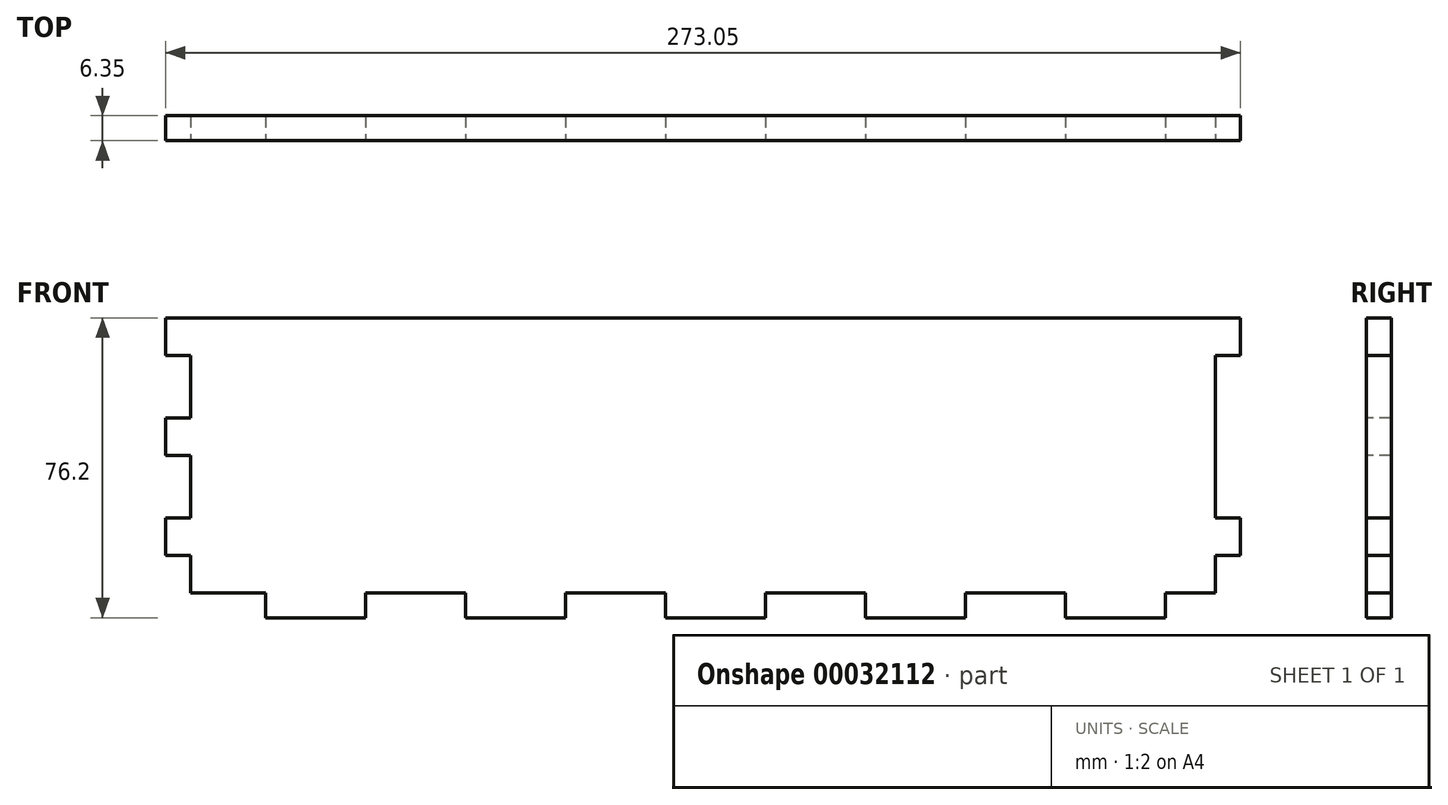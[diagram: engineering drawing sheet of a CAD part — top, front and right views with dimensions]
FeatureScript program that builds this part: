
annotation { "Feature Type Name" : "Feature", "Feature Type Description" : "" }
export const myFeature = defineFeature(function(context is Context, id is Id, definition is map)
    precondition{}
    {
        {
            var Q0;
            Q0=qCreatedBy(makeId("Front.planeOp"),FACE);
            var sketch = newSketch(context, id + "F0", { "sketchPlane" : qUnion([Q0])});
            skLineSegment(sketch, "E0.bottom", {"start": v(0, 0) * mm, "end": v(273.05, 0) * mm});
            skLineSegment(sketch, "E0.top", {"start": v(0, 76.2) * mm, "end": v(273.05, 76.2) * mm});
            skLineSegment(sketch, "E0.left", {"start": v(0, 0) * mm, "end": v(0, 76.2) * mm});
            skLineSegment(sketch, "E0.right", {"start": v(273.05, 0) * mm, "end": v(273.05, 76.2) * mm});
            skSolve(sketch);
        }
        {
            var Q0;
            Q0=makeQuery(id+"F0.imprint","IMPRINT",FACE,{"disambiguationData":[TD([[makeQuery(id+"F0.imprint","IMPRINT",EDGE,{"derivedFrom":sQuery(id+"F0.wireOp",EDGE,"E0.bottom")}),1.0]])]});
            extrude(context, id + "F1", {"entities" : qUnion([Q0]), "depth" : 6.35 * mm});
        }
        {
            var Q0;
            Q0=makeQuery(id+"F1.opExtrude","CAP_FACE",FACE,{"disambiguationData":[OSD([sQuery(id+"F0.wireOp",EDGE,"E0.bottom"),sQuery(id+"F0.wireOp",EDGE,"E0.top"),sQuery(id+"F0.wireOp",EDGE,"E0.left"),sQuery(id+"F0.wireOp",EDGE,"E0.right")])],"isStart":false});
            var sketch = newSketch(context, id + "F2", { "sketchPlane" : qUnion([Q0])});
            skLineSegment(sketch, "E1.bottom", {"start": v(0, 66.68) * mm, "end": v(6.35, 66.68) * mm});
            skLineSegment(sketch, "E1.top", {"start": v(0, 50.8) * mm, "end": v(6.35, 50.8) * mm});
            skLineSegment(sketch, "E1.left", {"start": v(0, 66.68) * mm, "end": v(0, 50.8) * mm});
            skLineSegment(sketch, "E1.right", {"start": v(6.35, 66.68) * mm, "end": v(6.35, 50.8) * mm});
            skLineSegment(sketch, "E2.bottom", {"start": v(0, 41.28) * mm, "end": v(6.35, 41.28) * mm});
            skLineSegment(sketch, "E2.top", {"start": v(0, 25.4) * mm, "end": v(6.35, 25.4) * mm});
            skLineSegment(sketch, "E2.left", {"start": v(0, 41.28) * mm, "end": v(0, 25.4) * mm});
            skLineSegment(sketch, "E2.right", {"start": v(6.35, 41.28) * mm, "end": v(6.35, 25.4) * mm});
            skLineSegment(sketch, "E3.bottom", {"start": v(0, 15.88) * mm, "end": v(6.35, 15.88) * mm});
            skLineSegment(sketch, "E3.top", {"start": v(0, 6.35) * mm, "end": v(6.35, 6.35) * mm});
            skLineSegment(sketch, "E3.left", {"start": v(0, 15.88) * mm, "end": v(0, 6.35) * mm});
            skLineSegment(sketch, "E3.right", {"start": v(6.35, 15.88) * mm, "end": v(6.35, 6.35) * mm});
            skLineSegment(sketch, "E4", {"start": v(136.53, 76.2) * mm, "end": v(136.53, 0) * mm, "construction": true});
            skLineSegment(sketch, "E5.MirrorCS", {"start": v(266.7, 15.88) * mm, "end": v(266.7, 6.35) * mm});
            skLineSegment(sketch, "E6.MirrorCS", {"start": v(273.05, 15.88) * mm, "end": v(273.05, 6.35) * mm});
            skLineSegment(sketch, "E7.MirrorCS", {"start": v(273.05, 6.35) * mm, "end": v(266.7, 6.35) * mm});
            skLineSegment(sketch, "E8.MirrorCS", {"start": v(273.05, 15.88) * mm, "end": v(266.7, 15.88) * mm});
            skLineSegment(sketch, "E9.MirrorCS", {"start": v(273.05, 41.28) * mm, "end": v(266.7, 41.28) * mm});
            skLineSegment(sketch, "E10.MirrorCS", {"start": v(273.05, 25.4) * mm, "end": v(266.7, 25.4) * mm});
            skLineSegment(sketch, "E11.MirrorCS", {"start": v(273.05, 66.68) * mm, "end": v(266.7, 66.68) * mm});
            skLineSegment(sketch, "E12.MirrorCS", {"start": v(273.05, 50.8) * mm, "end": v(266.7, 50.8) * mm});
            skLineSegment(sketch, "E13.MirrorCS", {"start": v(266.7, 41.28) * mm, "end": v(266.7, 25.4) * mm});
            skLineSegment(sketch, "E14.MirrorCS", {"start": v(273.05, 41.28) * mm, "end": v(273.05, 25.4) * mm});
            skLineSegment(sketch, "E15.MirrorCS", {"start": v(266.7, 66.68) * mm, "end": v(266.7, 50.8) * mm});
            skLineSegment(sketch, "E16.MirrorCS", {"start": v(273.05, 66.68) * mm, "end": v(273.05, 50.8) * mm});
            skSolve(sketch);
        }
        {
            var Q0;
            Q0=qSketchRegion(id+"F2",true);
            extrude(context, id + "F3", {"entities" : qUnion([Q0]), "operationType" : NewBodyOperationType.REMOVE, "endBound" : BoundingType.UP_TO_NEXT, "oppositeDirection" : true, "depth" : 25.4 * mm});
        }
        {
            var Q0;
            Q0=makeQuery(id+"F1.opExtrude","CAP_FACE",FACE,{"disambiguationData":[OSD([sQuery(id+"F0.wireOp",EDGE,"E0.bottom"),sQuery(id+"F0.wireOp",EDGE,"E0.top"),sQuery(id+"F0.wireOp",EDGE,"E0.left"),sQuery(id+"F0.wireOp",EDGE,"E0.right")])],"isStart":false});
            var sketch = newSketch(context, id + "F4", { "sketchPlane" : qUnion([Q0])});
            skLineSegment(sketch, "E17.bottom", {"start": v(0, 0) * mm, "end": v(25.4, 0) * mm});
            skLineSegment(sketch, "E17.top", {"start": v(0, 6.35) * mm, "end": v(25.4, 6.35) * mm});
            skLineSegment(sketch, "E17.left", {"start": v(0, 0) * mm, "end": v(0, 6.35) * mm});
            skLineSegment(sketch, "E17.right", {"start": v(25.4, 0) * mm, "end": v(25.4, 6.35) * mm});
            skLineSegment(sketch, "E18.1.0.0", {"start": v(76.2, 0) * mm, "end": v(76.2, 6.35) * mm});
            skLineSegment(sketch, "E18.1.0.1", {"start": v(50.8, 0) * mm, "end": v(50.8, 6.35) * mm});
            skLineSegment(sketch, "E18.1.0.2", {"start": v(50.8, 6.35) * mm, "end": v(76.2, 6.35) * mm});
            skLineSegment(sketch, "E18.1.0.3", {"start": v(50.8, 0) * mm, "end": v(76.2, 0) * mm});
            skLineSegment(sketch, "E18.2.0.0", {"start": v(127, 0) * mm, "end": v(127, 6.35) * mm});
            skLineSegment(sketch, "E18.2.0.1", {"start": v(101.6, 0) * mm, "end": v(101.6, 6.35) * mm});
            skLineSegment(sketch, "E18.2.0.2", {"start": v(101.6, 6.35) * mm, "end": v(127, 6.35) * mm});
            skLineSegment(sketch, "E18.2.0.3", {"start": v(101.6, 0) * mm, "end": v(127, 0) * mm});
            skLineSegment(sketch, "E18.3.0.0", {"start": v(177.8, 0) * mm, "end": v(177.8, 6.35) * mm});
            skLineSegment(sketch, "E18.3.0.1", {"start": v(152.4, 0) * mm, "end": v(152.4, 6.35) * mm});
            skLineSegment(sketch, "E18.3.0.2", {"start": v(152.4, 6.35) * mm, "end": v(177.8, 6.35) * mm});
            skLineSegment(sketch, "E18.3.0.3", {"start": v(152.4, 0) * mm, "end": v(177.8, 0) * mm});
            skLineSegment(sketch, "E18.4.0.0", {"start": v(228.6, 0) * mm, "end": v(228.6, 6.35) * mm});
            skLineSegment(sketch, "E18.4.0.1", {"start": v(203.2, 0) * mm, "end": v(203.2, 6.35) * mm});
            skLineSegment(sketch, "E18.4.0.2", {"start": v(203.2, 6.35) * mm, "end": v(228.6, 6.35) * mm});
            skLineSegment(sketch, "E18.4.0.3", {"start": v(203.2, 0) * mm, "end": v(228.6, 0) * mm});
            skLineSegment(sketch, "E18.direction1", {"start": v(25.4, 0) * mm, "end": v(76.2, 0) * mm, "construction": true});
            skLineSegment(sketch, "E19.0.5.0", {"start": v(279.4, 0) * mm, "end": v(279.4, 6.35) * mm});
            skLineSegment(sketch, "E19.3.5.0", {"start": v(254, 0) * mm, "end": v(254, 6.35) * mm});
            skLineSegment(sketch, "E19.6.5.0", {"start": v(254, 6.35) * mm, "end": v(279.4, 6.35) * mm});
            skLineSegment(sketch, "E19.9.5.0", {"start": v(254, 0) * mm, "end": v(279.4, 0) * mm});
            skSolve(sketch);
        }
        {
            var Q0;
            Q0=qSketchRegion(id+"F4",true);
            extrude(context, id + "F5", {"entities" : qUnion([Q0]), "operationType" : NewBodyOperationType.REMOVE, "endBound" : BoundingType.THROUGH_ALL, "oppositeDirection" : true, "depth" : 25.4 * mm});
        }
        {
            var Q0;
            Q0=makeQuery(id+"F1.opExtrude","CAP_FACE",FACE,{"disambiguationData":[OSD([sQuery(id+"F0.wireOp",EDGE,"E0.bottom"),sQuery(id+"F0.wireOp",EDGE,"E0.top"),sQuery(id+"F0.wireOp",EDGE,"E0.left"),sQuery(id+"F0.wireOp",EDGE,"E0.right")])],"isStart":false});
            var sketch = newSketch(context, id + "F6", { "sketchPlane" : qUnion([Q0])});
            skLineSegment(sketch, "E20.bottom", {"start": v(266.7, 41.28) * mm, "end": v(273.05, 41.28) * mm});
            skLineSegment(sketch, "E20.top", {"start": v(266.7, 50.8) * mm, "end": v(273.05, 50.8) * mm});
            skLineSegment(sketch, "E20.left", {"start": v(266.7, 41.28) * mm, "end": v(266.7, 50.8) * mm});
            skLineSegment(sketch, "E20.right", {"start": v(273.05, 41.28) * mm, "end": v(273.05, 50.8) * mm});
            skSolve(sketch);
        }
        {
            var Q0;
            Q0=qSketchRegion(id+"F6",true);
            extrude(context, id + "F7", {"entities" : qUnion([Q0]), "operationType" : NewBodyOperationType.REMOVE, "endBound" : BoundingType.UP_TO_NEXT, "oppositeDirection" : true, "depth" : 25.4 * mm});
        }
    });
